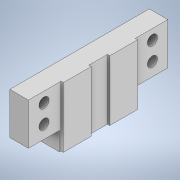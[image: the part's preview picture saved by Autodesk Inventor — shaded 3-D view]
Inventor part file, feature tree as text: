
AUTODESK INVENTOR PART (.ipt)
format: ipt  version: 2020 (Build 240168000, 168)  size: 176,640 bytes
history: native  units: mm
features: extrude x3, sketch x2, other x1
ambient origin geometry x8: Origin, YZ Plane, XZ Plane, XY Plane, X Axis, Y Axis, Z Axis, Center Point
bodies: Body1 (feature_tree)
feature tree (6):
  other  "Bryła1"
  extrude  "Wyciągnięcie proste1"  Depth=90.0mm
  sketch  "Szkic2"
  extrude  "Wyciągnięcie proste2"  Depth=12.0mm
  extrude  "Wyciągnięcie proste3"  Depth=45.0mm
  sketch  "Szkic1"
